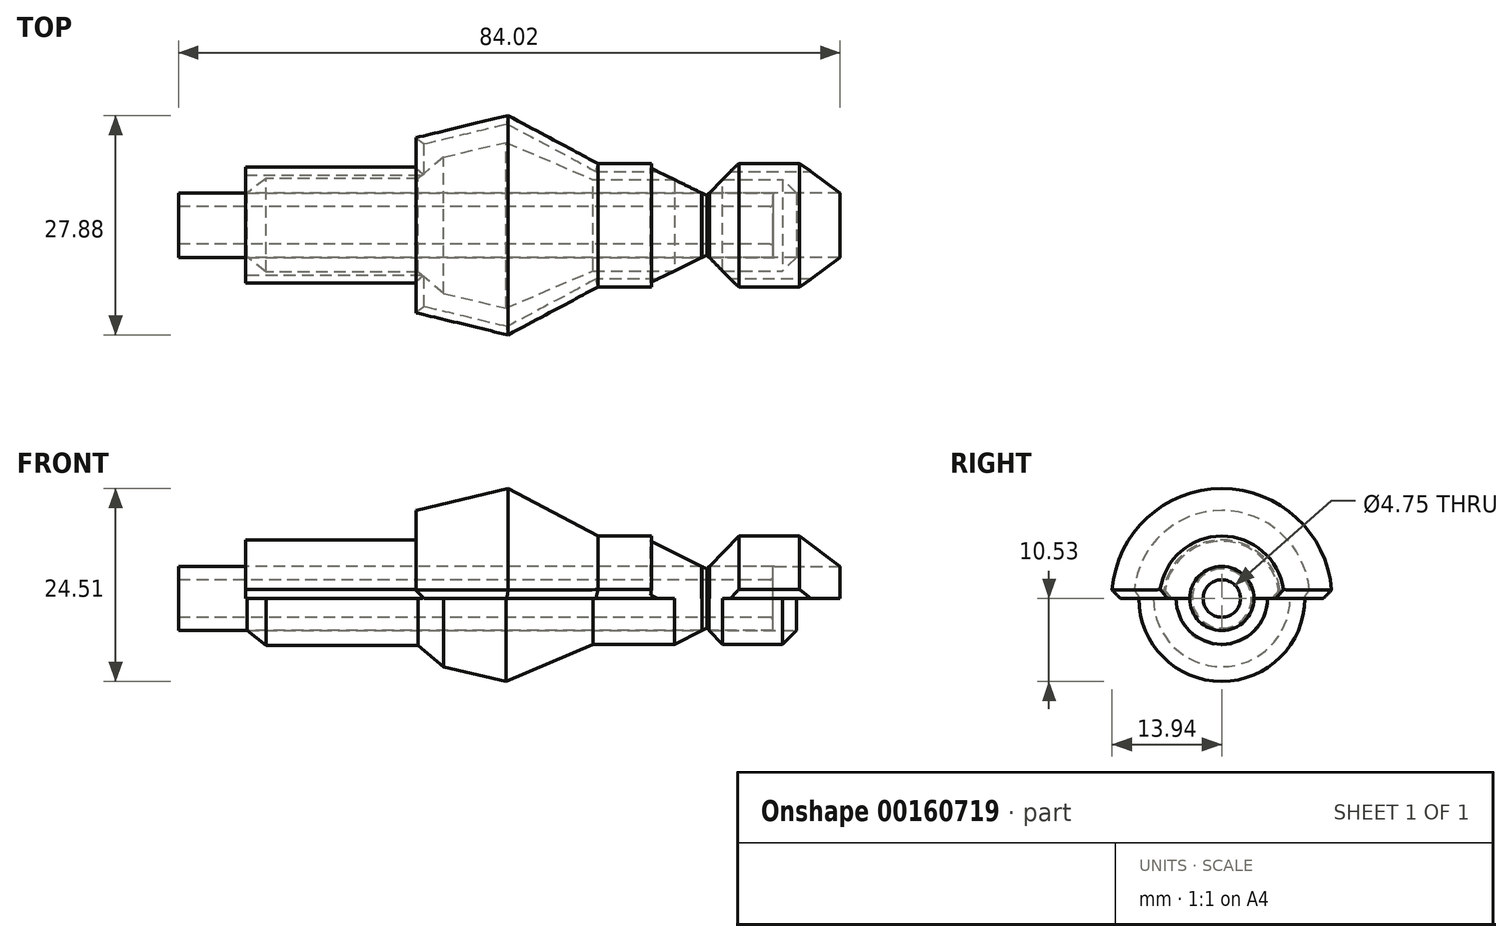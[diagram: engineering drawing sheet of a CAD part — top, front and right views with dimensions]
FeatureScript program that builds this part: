
annotation { "Feature Type Name" : "Feature", "Feature Type Description" : "" }
export const myFeature = defineFeature(function(context is Context, id is Id, definition is map)
    precondition{}
    {
        {
            var Q0;
            Q0=qCreatedBy(makeId("Right.planeOp"),FACE);
            var sketch = newSketch(context, id + "F0", { "sketchPlane" : qUnion([Q0])});
            skCircle(sketch, "E0", {"center": v(0, 0) * mm, "radius": 4.08 * mm});
            skSolve(sketch);
        }
        {
            var Q0;
            Q0 = qSketchRegion(id + "F0", true);
            extrude(context, id + "F1", {"entities" : qUnion([Q0]), "depth" : 75.25 * mm});
        }
        {
            var Q0;
            Q0=qCreatedBy(makeId("Front.planeOp"),FACE);
            var sketch = newSketch(context, id + "F2", { "sketchPlane" : qUnion([Q0])});
            skLineSegment(sketch, "E1", {"start": v(8.24, 4.08) * mm, "end": v(8.24, 7.46) * mm});
            skLineSegment(sketch, "E2", {"start": v(8.24, 7.46) * mm, "end": v(29.95, 7.46) * mm});
            skLineSegment(sketch, "E3", {"start": v(29.95, 7.46) * mm, "end": v(29.95, 11.18) * mm});
            skLineSegment(sketch, "E4", {"start": v(29.95, 11.18) * mm, "end": v(41.6, 13.98) * mm});
            skLineSegment(sketch, "E5", {"start": v(41.6, 13.98) * mm, "end": v(53.01, 7.92) * mm});
            skLineSegment(sketch, "E6", {"start": v(53.01, 7.92) * mm, "end": v(78.64, 7.92) * mm});
            skLineSegment(sketch, "E7", {"start": v(78.64, 7.92) * mm, "end": v(83.77, 4.08) * mm});
            skLineSegment(sketch, "E8", {"start": v(83.77, 4.08) * mm, "end": v(75.45, 4.08) * mm});
            skLineSegment(sketch, "E9", {"start": v(8.24, 4.08) * mm, "end": v(75.45, 4.08) * mm});
            skSolve(sketch);
        }
        {
            var Q0;
            Q0=qCreatedBy(makeId("Front.planeOp"),FACE);
            var sketch = newSketch(context, id + "F3", { "sketchPlane" : qUnion([Q0])});
            skLineSegment(sketch, "E10", {"start": v(41.03, 13.4) * mm, "end": v(41.03, 0) * mm});
            skLineSegment(sketch, "E11", {"start": v(41.03, 0) * mm, "end": v(75.21, 0) * mm});
            skLineSegment(sketch, "E12", {"start": v(75.21, 0) * mm, "end": v(0, 0) * mm});
            skSolve(sketch);
        }
        {
            var Q0;
            Q0=makeQuery(id+"F2.imprint","IMPRINT",FACE,{"disambiguationData":[TD([[makeQuery(id+"F2.imprint","IMPRINT",EDGE,{"derivedFrom":sQuery(id+"F2.wireOp",EDGE,"E1")}),-1.0]])]});
            var Q1;
            Q1=sQuery(id+"F3.wireOp",EDGE,"E12");
            revolve(context, id + "F4", {"entities" : qUnion([Q0]), "axis" : qUnion([Q1]), "revolveType" : RevolveType.TWO_DIRECTIONS, "angle" : 90 * degree, "angleBack" : 270 * degree});
        }
        {
            var Q0;
            Q0=qCreatedBy(makeId("Top.planeOp"),FACE);
            var sketch = newSketch(context, id + "F5", { "sketchPlane" : qUnion([Q0])});
            skLineSegment(sketch, "E13", {"start": v(33.4, -8.66) * mm, "end": v(41.34, -10.53) * mm});
            skLineSegment(sketch, "E14", {"start": v(41.34, -10.53) * mm, "end": v(52.37, -5.8) * mm});
            skLineSegment(sketch, "E15", {"start": v(52.37, -5.8) * mm, "end": v(78.5, -5.8) * mm});
            skLineSegment(sketch, "E16", {"start": v(78.5, -5.8) * mm, "end": v(78.5, -4.08) * mm});
            skLineSegment(sketch, "E17", {"start": v(78.5, -4.08) * mm, "end": v(33.4, -4.08) * mm});
            skLineSegment(sketch, "E18", {"start": v(33.4, -8.66) * mm, "end": v(30.2, -5.94) * mm});
            skLineSegment(sketch, "E19", {"start": v(30.2, -5.94) * mm, "end": v(10.84, -5.94) * mm});
            skLineSegment(sketch, "E20", {"start": v(10.84, -5.94) * mm, "end": v(8.49, -4.08) * mm});
            skLineSegment(sketch, "E21", {"start": v(8.49, -4.08) * mm, "end": v(33.4, -4.08) * mm});
            skSolve(sketch);
        }
        {
            var Q0;
            Q0=makeQuery(id+"F5.imprint","IMPRINT",FACE,{"disambiguationData":[TD([[makeQuery(id+"F5.imprint","IMPRINT",EDGE,{"derivedFrom":sQuery(id+"F5.wireOp",EDGE,"E13")}),1.0]])]});
            var Q1;
            Q1=sQuery(id+"F3.wireOp",EDGE,"E12");
            revolve(context, id + "F6", {"operationType" : NewBodyOperationType.ADD, "entities" : qUnion([Q0]), "axis" : qUnion([Q1]), "revolveType" : RevolveType.TWO_DIRECTIONS, "angle" : 360 * degree, "angleBack" : 180 * degree});
        }
        {
            var Q0;
            Q0=makeQuery(id+"F1.opExtrude","CAP_FACE",FACE,{"disambiguationData":[OSD([sQuery(id+"F0.wireOp",EDGE,"E0")])],"isStart":true});
            var Q1;
            Q1=makeQuery(id+"F1.opExtrude","CAP_FACE",FACE,{"disambiguationData":[OSD([sQuery(id+"F0.wireOp",EDGE,"E0")])],"isStart":false});
            shell(context, id + "F7", {"entities" : qUnion([Q0, Q1]), "thickness" : 1.7 * mm});
        }
        {
            var Q0;
            Q0=makeQuery(id+"F4.opRevolve","CAP_EDGE",EDGE,{"disambiguationData":[OSD([sQuery(id+"F2.wireOp",EDGE,"E6")])],"isStart":true});
            var Q1;
            Q1=makeQuery(id+"F4.opRevolve","CAP_EDGE",EDGE,{"disambiguationData":[OSD([sQuery(id+"F2.wireOp",EDGE,"E5")])],"isStart":true});
            var Q2;
            Q2=makeQuery(id+"F4.opRevolve","CAP_EDGE",EDGE,{"disambiguationData":[OSD([sQuery(id+"F2.wireOp",EDGE,"E4")])],"isStart":true});
            var Q3;
            Q3=makeQuery(id+"F4.opRevolve","CAP_EDGE",EDGE,{"disambiguationData":[OSD([sQuery(id+"F2.wireOp",EDGE,"E3")])],"isStart":true});
            var Q4;
            Q4=makeQuery(id+"F4.opRevolve","CAP_EDGE",EDGE,{"disambiguationData":[OSD([sQuery(id+"F2.wireOp",EDGE,"E2")])],"isStart":true});
            chamfer(context, id + "F8", {"entities" : qUnion([Q0, Q1, Q2, Q3, Q4]), "width" : 1 * mm, "tangentPropagation" : true});
        }
        {
            var Q0;
            Q0=makeQuery(id+"F4.opRevolve","CAP_EDGE",EDGE,{"disambiguationData":[OSD([sQuery(id+"F2.wireOp",EDGE,"E6")])],"isStart":false});
            var Q1;
            Q1=makeQuery(id+"F4.opRevolve","CAP_EDGE",EDGE,{"disambiguationData":[OSD([sQuery(id+"F2.wireOp",EDGE,"E5")])],"isStart":false});
            var Q2;
            Q2=makeQuery(id+"F4.opRevolve","CAP_EDGE",EDGE,{"disambiguationData":[OSD([sQuery(id+"F2.wireOp",EDGE,"E4")])],"isStart":false});
            var Q3;
            Q3=makeQuery(id+"F4.opRevolve","CAP_EDGE",EDGE,{"disambiguationData":[OSD([sQuery(id+"F2.wireOp",EDGE,"E3")])],"isStart":false});
            var Q4;
            Q4=makeQuery(id+"F4.opRevolve","CAP_EDGE",EDGE,{"disambiguationData":[OSD([sQuery(id+"F2.wireOp",EDGE,"E2")])],"isStart":false});
            chamfer(context, id + "F9", {"entities" : qUnion([Q0, Q1, Q2, Q3, Q4]), "width" : 1 * mm, "tangentPropagation" : true});
        }
        {
            var Q0;
            Q0=makeQuery(id+"F6.opRevolve","SWEPT_EDGE",EDGE,{"disambiguationData":[OSD([sQuery(id+"F5.wireOp",EDGE,"E15"),sQuery(id+"F5.wireOp",EDGE,"E16")])]});
            chamfer(context, id + "F10", {"entities" : qUnion([Q0]), "width" : 2 * mm, "tangentPropagation" : true});
        }
        {
            var Q0;
            {var subQ0=sQuery(id+"F0.wireOp",EDGE,"E0");Q0=makeQuery(id+"F7.opShell","OFFSET_EDGE",EDGE,{"disambiguationData":[OSD([subQ0]),TDD([makeQuery(id+"F1.opExtrude","CAP_EDGE",EDGE,{"disambiguationData":[OSD([subQ0])],"isStart":false})])]});}
            fillet(context, id + "F11", {"entities" : qUnion([Q0]), "radius" : 0.4 * mm, "tangentPropagation" : true, "allowEdgeOverflow" : false});
        }
        {
            var Q0;
            Q0=qCreatedBy(makeId("Front.planeOp"),FACE);
            var sketch = newSketch(context, id + "F12", { "sketchPlane" : qUnion([Q0])});
            skCircle(sketch, "E22.cCircle", {"center": v(65.71, 10.42) * mm, "radius": 5.47 * mm, "construction": true});
            skLineSegment(sketch, "E22.0", {"start": v(59.73, 7.28) * mm, "end": v(60.87, 15.14) * mm});
            skLineSegment(sketch, "E22.1", {"start": v(60.87, 15.14) * mm, "end": v(68.7, 16.48) * mm});
            skLineSegment(sketch, "E22.2", {"start": v(68.7, 16.48) * mm, "end": v(72.4, 9.45) * mm});
            skLineSegment(sketch, "E22.3", {"start": v(72.4, 9.45) * mm, "end": v(66.85, 3.76) * mm});
            skLineSegment(sketch, "E22.4", {"start": v(66.85, 3.76) * mm, "end": v(59.73, 7.28) * mm});
            skPoint(sketch, "E22.0.midPoint", {"position": v(60.3, 11.2) * mm});
            skSolve(sketch);
        }
        {
            var Q0;
            Q0=makeQuery(id+"F12.imprint","IMPRINT",FACE,{"disambiguationData":[TD([[makeQuery(id+"F12.imprint","IMPRINT",EDGE,{"derivedFrom":sQuery(id+"F12.wireOp",EDGE,"E22.0")}),-1.0]])]});
            var Q1;
            Q1=sQuery(id+"F3.wireOp",EDGE,"E12");
            revolve(context, id + "F13", {"operationType" : NewBodyOperationType.REMOVE, "entities" : qUnion([Q0]), "axis" : qUnion([Q1]), "revolveType" : RevolveType.FULL, "oppositeDirection" : true});
        }
        {
            var Q0;
            Q0=makeQuery(id+"F1.opExtrude","CAP_FACE",FACE,{"disambiguationData":[OSD([sQuery(id+"F0.wireOp",EDGE,"E0")])],"isStart":true});
            extrude(context, id + "F14", {"entities" : qUnion([Q0]), "operationType" : NewBodyOperationType.ADD, "depth" : 0.25 * mm});
        }
    });
